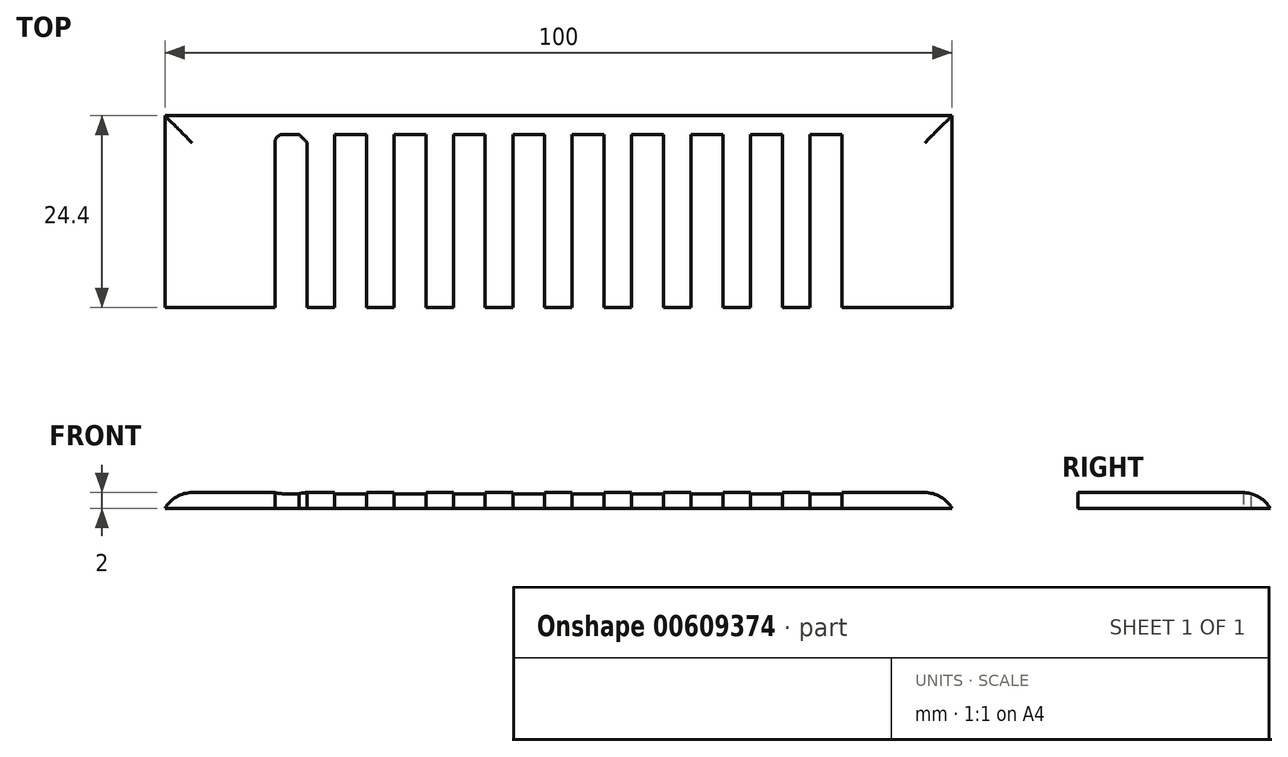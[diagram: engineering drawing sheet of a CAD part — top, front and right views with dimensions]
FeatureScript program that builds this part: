
annotation { "Feature Type Name" : "Feature", "Feature Type Description" : "" }
export const myFeature = defineFeature(function(context is Context, id is Id, definition is map)
    precondition{}
    {
        {
            var Q0;
            Q0=qCreatedBy(makeId("Top.planeOp"),FACE);
            var sketch = newSketch(context, id + "F0", { "sketchPlane" : qUnion([Q0])});
            skLineSegment(sketch, "E0", {"start": v(0, 0) * mm, "end": v(-1.75, 0) * mm});
            skLineSegment(sketch, "E1", {"start": v(-1.75, 0) * mm, "end": v(-1.75, 22) * mm});
            skLineSegment(sketch, "E2", {"start": v(-1.75, 22) * mm, "end": v(-5.8, 22) * mm});
            skLineSegment(sketch, "E3", {"start": v(-5.8, 22) * mm, "end": v(-5.8, 0) * mm});
            skLineSegment(sketch, "E4", {"start": v(-5.8, 0) * mm, "end": v(-9.3, 0) * mm});
            skLineSegment(sketch, "E5", {"start": v(-9.3, 0) * mm, "end": v(-9.3, 22) * mm});
            skLineSegment(sketch, "E6", {"start": v(-9.3, 22) * mm, "end": v(-13.35, 22) * mm});
            skLineSegment(sketch, "E7", {"start": v(-13.35, 22) * mm, "end": v(-13.35, 0) * mm});
            skLineSegment(sketch, "E8", {"start": v(-13.35, 0) * mm, "end": v(-16.85, 0) * mm});
            skLineSegment(sketch, "E9", {"start": v(-16.85, 0) * mm, "end": v(-16.85, 22) * mm});
            skLineSegment(sketch, "E10", {"start": v(-16.85, 22) * mm, "end": v(-20.9, 22) * mm});
            skLineSegment(sketch, "E11", {"start": v(-20.9, 22) * mm, "end": v(-20.9, 0) * mm});
            skLineSegment(sketch, "E12", {"start": v(-20.9, 0) * mm, "end": v(-24.4, 0) * mm});
            skLineSegment(sketch, "E13", {"start": v(-24.4, 0) * mm, "end": v(-24.4, 22) * mm});
            skLineSegment(sketch, "E14", {"start": v(-24.4, 22) * mm, "end": v(-28.45, 22) * mm});
            skLineSegment(sketch, "E15", {"start": v(-28.45, 22) * mm, "end": v(-28.45, 0) * mm});
            skLineSegment(sketch, "E16", {"start": v(-28.45, 0) * mm, "end": v(-31.95, 0) * mm});
            skLineSegment(sketch, "E17", {"start": v(-31.95, 0) * mm, "end": v(-31.95, 22) * mm});
            skLineSegment(sketch, "E18", {"start": v(-31.95, 22) * mm, "end": v(-36, 22) * mm});
            skLineSegment(sketch, "E19", {"start": v(-36, 22) * mm, "end": v(-36, 0) * mm});
            skLineSegment(sketch, "E20", {"start": v(-36, 0) * mm, "end": v(-50, 0) * mm});
            skLineSegment(sketch, "E21", {"start": v(-50, 0) * mm, "end": v(-50, 24.4) * mm});
            skLineSegment(sketch, "E22", {"start": v(-50, 24.4) * mm, "end": v(0, 24.4) * mm});
            skLineSegment(sketch, "E23", {"start": v(0, 24.4) * mm, "end": v(0, 0) * mm});
            skSolve(sketch);
        }
        {
            var Q0;
            Q0=makeQuery(id+"F0.imprint","IMPRINT",FACE,{"disambiguationData":[TD([[makeQuery(id+"F0.imprint","IMPRINT",EDGE,{"derivedFrom":sQuery(id+"F0.wireOp",EDGE,"E0")}),-1.0]])]});
            extrude(context, id + "F1", {"entities" : qUnion([Q0]), "depth" : 2 * mm, "offsetDistance" : 25 * mm});
        }
        {
            var Q0;
            Q0=makeQuery(id+"F1.opExtrude","CAP_EDGE",EDGE,{"disambiguationData":[OSD([sQuery(id+"F0.wireOp",EDGE,"E22")])],"isStart":false});
            fillet(context, id + "F2", {"entities" : qUnion([Q0]), "radius" : 4 * mm, "tangentPropagation" : true, "allowEdgeOverflow" : false});
        }
        {
            var Q0;
            Q0=makeQuery(id+"F1.opExtrude","CAP_EDGE",EDGE,{"disambiguationData":[OSD([sQuery(id+"F0.wireOp",EDGE,"E21")])],"isStart":false});
            fillet(context, id + "F3", {"entities" : qUnion([Q0]), "radius" : 4 * mm, "tangentPropagation" : true, "allowEdgeOverflow" : false});
        }
        {
            var Q0;
            Q0=makeQuery(id+"F1.opExtrude","SWEPT_BODY",BODY,{"disambiguationData":[OSD([sQuery(id+"F0.wireOp",EDGE,"E0"),sQuery(id+"F0.wireOp",EDGE,"E1"),sQuery(id+"F0.wireOp",EDGE,"E2"),sQuery(id+"F0.wireOp",EDGE,"E3"),sQuery(id+"F0.wireOp",EDGE,"E4"),sQuery(id+"F0.wireOp",EDGE,"E5"),sQuery(id+"F0.wireOp",EDGE,"E6"),sQuery(id+"F0.wireOp",EDGE,"E7"),sQuery(id+"F0.wireOp",EDGE,"E8"),sQuery(id+"F0.wireOp",EDGE,"E9"),sQuery(id+"F0.wireOp",EDGE,"E10"),sQuery(id+"F0.wireOp",EDGE,"E11"),sQuery(id+"F0.wireOp",EDGE,"E12"),sQuery(id+"F0.wireOp",EDGE,"E13"),sQuery(id+"F0.wireOp",EDGE,"E14"),sQuery(id+"F0.wireOp",EDGE,"E15"),sQuery(id+"F0.wireOp",EDGE,"E16"),sQuery(id+"F0.wireOp",EDGE,"E17"),sQuery(id+"F0.wireOp",EDGE,"E18"),sQuery(id+"F0.wireOp",EDGE,"E19"),sQuery(id+"F0.wireOp",EDGE,"E20"),sQuery(id+"F0.wireOp",EDGE,"E21"),sQuery(id+"F0.wireOp",EDGE,"E22"),sQuery(id+"F0.wireOp",EDGE,"E23")])]});
            var Q1;
            Q1=qCreatedBy(makeId("Right.planeOp"),FACE);
            mirror(context, id + "F4", {"operationType" : NewBodyOperationType.ADD, "entities" : qUnion([Q0]), "mirrorPlane" : qUnion([Q1])});
        }
        {
            var Q0;
            Q0=makeQuery(id+"F1.opExtrude","SWEPT_EDGE",EDGE,{"disambiguationData":[OSD([sQuery(id+"F0.wireOp",EDGE,"E18"),sQuery(id+"F0.wireOp",EDGE,"E19")])]});
            fillet(context, id + "F5", {"entities" : qUnion([Q0]), "radius" : 1 * mm, "tangentPropagation" : true, "allowEdgeOverflow" : false});
        }
        {
            var Q0;
            Q0=makeQuery(id+"F1.opExtrude","SWEPT_EDGE",EDGE,{"disambiguationData":[OSD([sQuery(id+"F0.wireOp",EDGE,"E17"),sQuery(id+"F0.wireOp",EDGE,"E18")])]});
            chamfer(context, id + "F6", {"entities" : qUnion([Q0]), "width" : 1 * mm, "tangentPropagation" : true});
        }
    });
